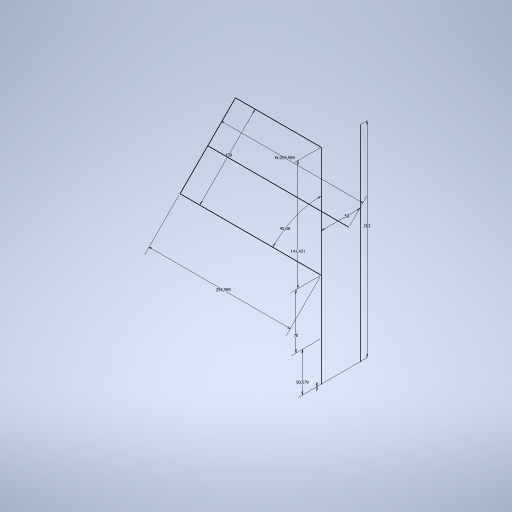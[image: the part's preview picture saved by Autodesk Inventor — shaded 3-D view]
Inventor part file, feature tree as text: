
AUTODESK INVENTOR PART (.ipt)
format: ipt  version: 2024.3 (Build 283343000, 343)  size: 244,224 bytes
history: native  units: mm
features: sketch x1
ambient origin geometry x8: Origin, YZ Plane, XZ Plane, XY Plane, X Axis, Y Axis, Z Axis, Center Point
feature tree (1):
  sketch  "Sketch1"  dims[d0=262.0mm d1=50.579mm d2=70.0mm d3=141.421mm d4=45.0deg d5=100.0mm d6=50.0mm d7=254.989146mm d8=254.989146mm d9=0.0mm]
